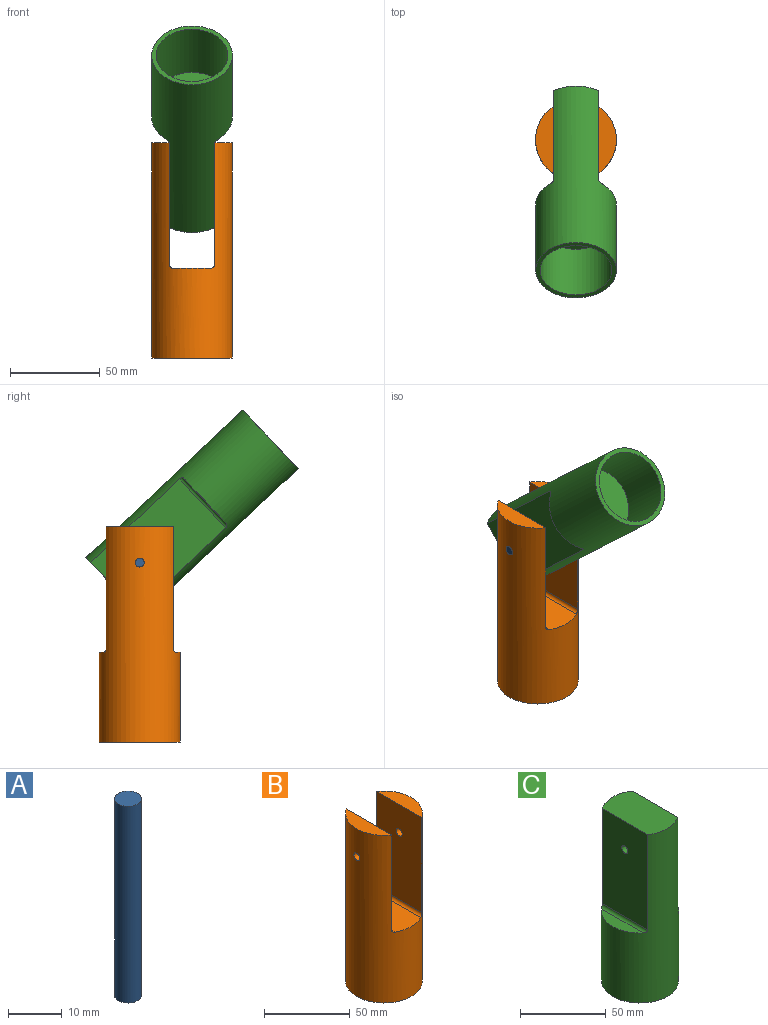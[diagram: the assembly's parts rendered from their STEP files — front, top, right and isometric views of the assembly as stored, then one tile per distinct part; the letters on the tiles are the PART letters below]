
ASSEMBLY  parts=3 mates=2
PART A: 3 faces, bbox 5x5x45 mm
  f0: cylinder r=2.5mm len=45mm, axis (0,0,-1), area 706.9mm2, adj f1,f2
  f1: plane 5x5mm, normal (0,0,1), area 19.6mm2, adj f0
  f2: plane 5x5mm, normal (0,0,-1), area 19.6mm2, adj f0
PART B: 13 faces, bbox 45x45x120 mm
  f0: cylinder r=22.5mm len=120mm, axis (0,0,-1), area 13218.5mm2, adj f1,f2,f3,f4,f5,f6,f9,f10
  f1: plane 37.42x10mm, normal (0,0,1), area 263.2mm2, adj f0,f5
  f2: plane 37.42x10mm, normal (0,0,1), area 263.2mm2, adj f0,f4
  f3: plane 45x45mm, normal (0,0,-1), area 333.8mm2, adj f0,f7
  f4: plane 68x37.42mm, normal (1,0,0), area 2524.7mm2, adj f0,f2,f10,f11
  f5: plane 68x37.42mm, normal (-1,0,0), area 2524.7mm2, adj f0,f1,f9,f12
  f6: plane 45x21mm, normal (0,0,1), area 909.5mm2, adj f0,f11,f12
  f7: cylinder r=20mm len=40mm, axis (0,0,-1), area 4398.2mm2, adj f3,f8
  f8: plane 40x40mm, normal (0,0,-1), area 1256.6mm2, adj f7
  f9: cylinder r=2.5mm len=10mm, axis (1,0,0), area 156mm2, adj f0,f5
  f10: cylinder r=2.5mm len=10mm, axis (1,0,0), area 156mm2, adj f0,f4
  f11: cylinder r=2mm len=39.8mm, axis (0,-1,0), area 120.4mm2, adj f0,f4,f6
  f12: cylinder r=2mm len=39.8mm, axis (0,1,0), area 120.4mm2, adj f0,f5,f6
PART C: 12 faces, bbox 45x45x120 mm
  f0: plane 45x25mm, normal (0,0,1), area 1064.1mm2, adj f1,f3,f5
  f1: cylinder r=22.5mm len=120mm, axis (0,0,-1), area 10783.7mm2, adj f0,f2,f3,f4,f5,f6,f10,f11
  f2: plane 45x45mm, normal (0,0,-1), area 333.8mm2, adj f1,f7
  f3: plane 68x37.42mm, normal (-1,0,0), area 2524.7mm2, adj f0,f1,f9,f10
  f4: plane 34.41x8mm, normal (0,0,1), area 191.2mm2, adj f1,f10
  f5: plane 68x37.42mm, normal (1,0,0), area 2524.7mm2, adj f0,f1,f9,f11
  f6: plane 34.41x8mm, normal (0,0,1), area 191.2mm2, adj f1,f11
  f7: cylinder r=20mm len=40mm, axis (0,0,-1), area 4398.2mm2, adj f2,f8
  f8: plane 40x40mm, normal (0,0,-1), area 1256.6mm2, adj f7
  f9: cylinder r=2.5mm len=25mm, axis (1,0,0), area 392.7mm2, adj f3,f5
  f10: cylinder r=2mm len=37.42mm, axis (0,1,0), area 114.3mm2, adj f1,f3,f4
  f11: cylinder r=2mm len=37.42mm, axis (0,-1,0), area 114.3mm2, adj f1,f5,f6
PLACE A rot(axis=(0.71,0,0.71),180deg) t=(-81.66,-2.07,88.18)mm
PLACE B t=(-59.22,-2.07,-11.82)mm fixed
PLACE C rot(axis=(-1,0,0),133.3deg) t=(-59.16,-74.82,156.79)mm
MATE fastened B.f9 <-> A.f0  axis (1,0,0) through (-36.66,-2.07,88.18)mm
MATE revolute C.f9 <-> A.f0  axis (1,0,0) through (-59.16,-2.07,88.18)mm
